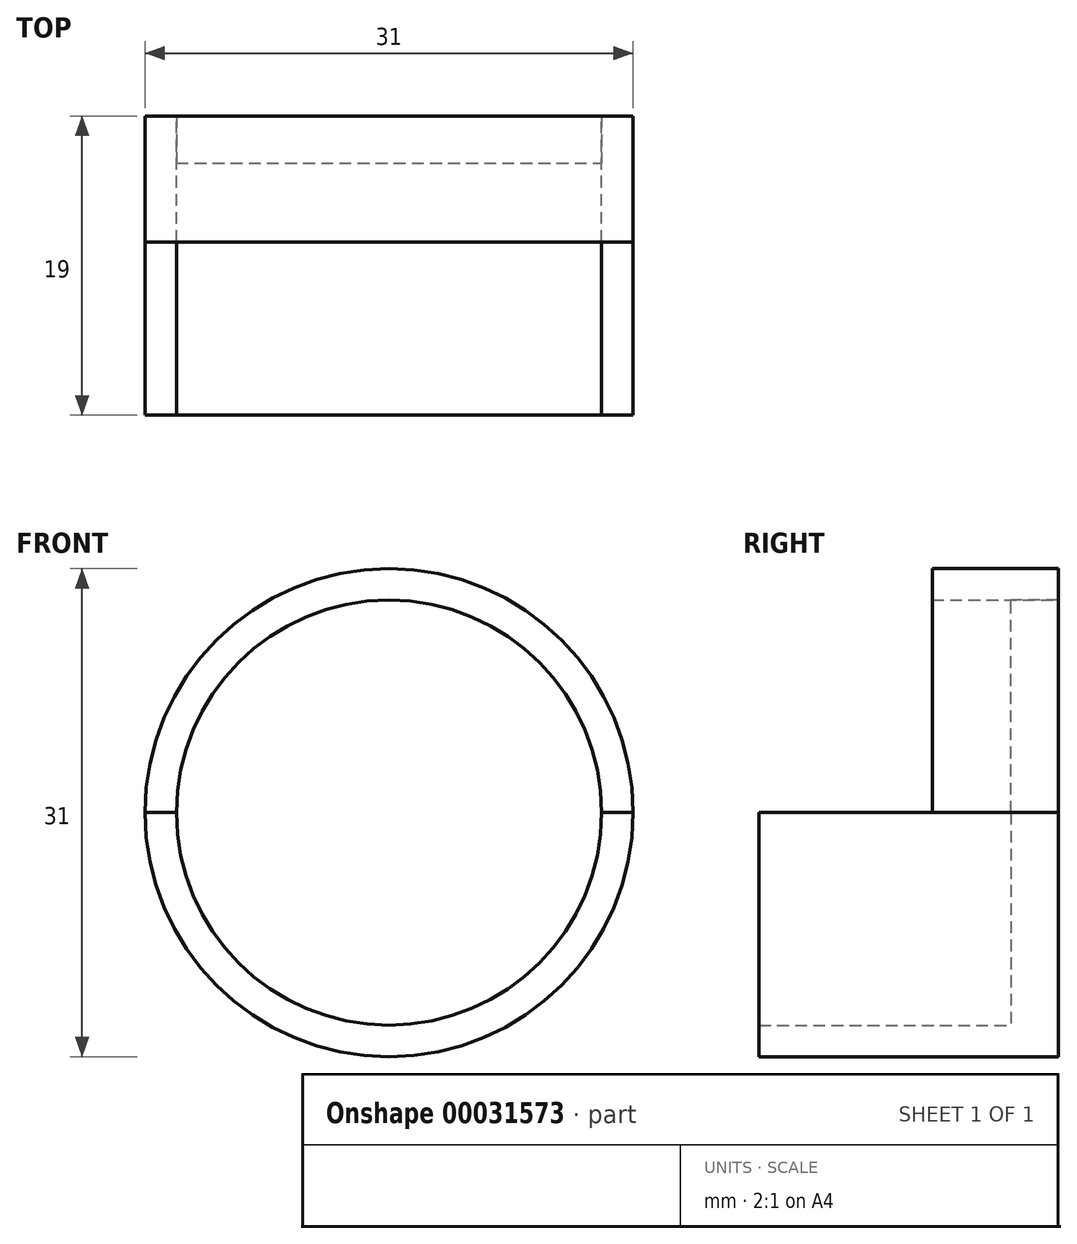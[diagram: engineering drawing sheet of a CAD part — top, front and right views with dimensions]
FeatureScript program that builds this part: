
annotation { "Feature Type Name" : "Feature", "Feature Type Description" : "" }
export const myFeature = defineFeature(function(context is Context, id is Id, definition is map)
    precondition{}
    {
        {
            var Q0;
            Q0=qCreatedBy(makeId("Front.planeOp"),FACE);
            var sketch = newSketch(context, id + "F0", { "sketchPlane" : qUnion([Q0])});
            skCircle(sketch, "E0", {"center": v(0, 0) * mm, "radius": 13.5 * mm});
            skArc(sketch, "E1", {"start": v(-15.5, 0) * mm, "mid": v(0, -15.5) * mm, "end": v(15.5, 0) * mm});
            skLineSegment(sketch, "E2", {"start": v(13.5, 0) * mm, "end": v(15.5, 0) * mm});
            skPoint(sketch, "E3.end.orphan", {"position": v(-13.5, 0) * mm});
            skLineSegment(sketch, "E4", {"start": v(-13.5, 0) * mm, "end": v(-15.5, 0) * mm});
            skSolve(sketch);
        }
        {
            var Q0;
            Q0=makeQuery(id+"F0.imprint","IMPRINT",FACE,{"disambiguationData":[TD([[makeQuery(id+"F0.imprint","IMPRINT",EDGE,{"derivedFrom":sQuery(id+"F0.wireOp",EDGE,"E1")}),1.0]])]});
            extrude(context, id + "F1", {"entities" : qUnion([Q0]), "depth" : 16 * mm});
        }
        {
            var Q0;
            Q0=makeQuery(id+"F0.imprint","IMPRINT",FACE,{"disambiguationData":[TD([[makeQuery(id+"F0.imprint","IMPRINT",EDGE,{"derivedFrom":sQuery(id+"F0.wireOp",EDGE,"E1")}),1.0]])]});
            var Q1;
            {var subQ0=sQuery(id+"F0.wireOp",EDGE,"E0");var subQ2=makeQuery(id+"F0.imprint","INTERSECT",VERTEX,{"derivedFrom":[subQ0,sQuery(id+"F0.wireOp",EDGE,"E2")]});Q1=makeQuery(id+"F0.imprint","IMPRINT",FACE,{"disambiguationData":[TD([[makeQuery(id+"F0.imprint","IMPRINT",EDGE,{"disambiguationData":[TD([[subQ2,-1.0]])],"derivedFrom":subQ0}),1.0]])]});}
            extrude(context, id + "F2", {"entities" : qUnion([Q0, Q1]), "operationType" : NewBodyOperationType.ADD, "oppositeDirection" : true, "depth" : 3 * mm});
        }
        {
            var Q0;
            Q0=makeQuery(id+"F2.opExtrude","CAP_FACE",FACE,{"disambiguationData":[OSD([sQuery(id+"F0.wireOp",EDGE,"E0"),sQuery(id+"F0.wireOp",EDGE,"E1"),sQuery(id+"F0.wireOp",EDGE,"E2"),sQuery(id+"F0.wireOp",EDGE,"E4")])],"isStart":false});
            var sketch = newSketch(context, id + "F3", { "sketchPlane" : qUnion([Q0])});
            skCircle(sketch, "E5", {"center": v(0, 0) * mm, "radius": 15.5 * mm});
            skPoint(sketch, "E5.first.point", {"position": v(-15.5, 0) * mm});
            skPoint(sketch, "E5.second.point", {"position": v(15.5, 0) * mm});
            skPoint(sketch, "E5.third.point", {"position": v(-0.94, -15.47) * mm});
            skArc(sketch, "E6", {"start": v(13.5, 0) * mm, "mid": v(0, 13.5) * mm, "end": v(-13.5, 0) * mm});
            skLineSegment(sketch, "E7", {"start": v(-15.5, 0) * mm, "end": v(-13.5, 0) * mm});
            skLineSegment(sketch, "E8", {"start": v(13.5, 0) * mm, "end": v(15.5, 0) * mm});
            skSolve(sketch);
        }
        {
            var Q0;
            Q0=makeQuery(id+"F3.imprint","IMPRINT",FACE,{"disambiguationData":[TD([[makeQuery(id+"F3.imprint","IMPRINT",EDGE,{"disambiguationData":[OD(0.0)],"derivedFrom":sQuery(id+"F3.wireOp",EDGE,"E5")}),1.0]])]});
            extrude(context, id + "F4", {"entities" : qUnion([Q0]), "oppositeDirection" : true, "depth" : 8 * mm});
        }
    });
